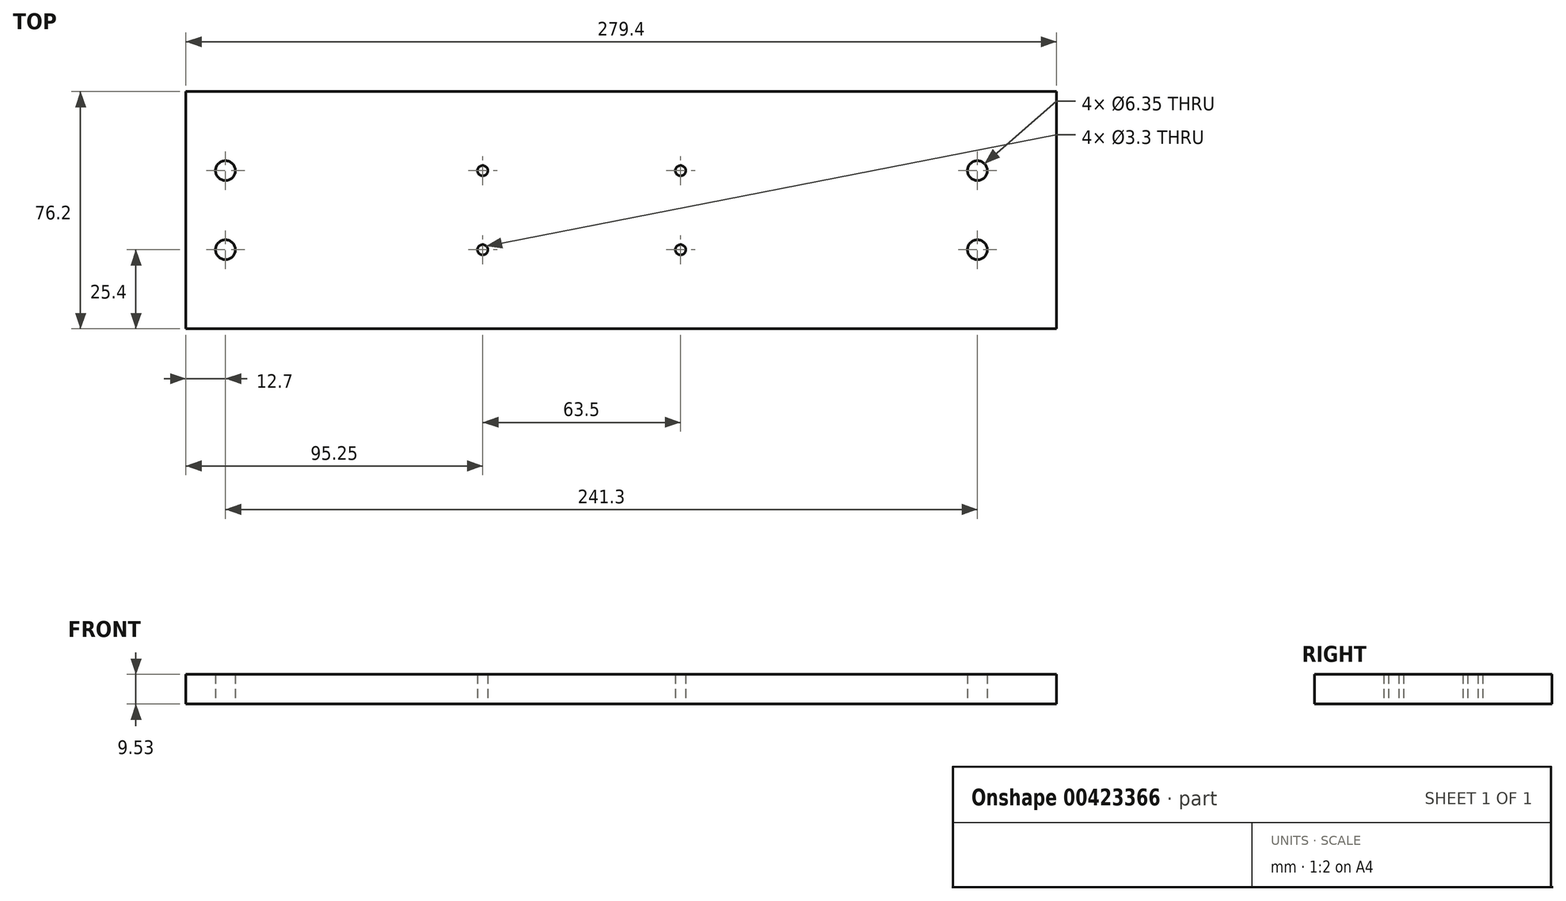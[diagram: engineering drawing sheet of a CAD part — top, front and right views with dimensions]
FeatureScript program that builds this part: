
annotation { "Feature Type Name" : "Feature", "Feature Type Description" : "" }
export const myFeature = defineFeature(function(context is Context, id is Id, definition is map)
    precondition{}
    {
        {
            var Q0;
            Q0=qCreatedBy(makeId("Top.planeOp"),FACE);
            var sketch = newSketch(context, id + "F0", { "sketchPlane" : qUnion([Q0])});
            skLineSegment(sketch, "E0.bottom", {"start": v(-139.7, 38.1) * mm, "end": v(139.7, 38.1) * mm});
            skLineSegment(sketch, "E0.top", {"start": v(-139.7, -38.1) * mm, "end": v(139.7, -38.1) * mm});
            skLineSegment(sketch, "E0.left", {"start": v(-139.7, 38.1) * mm, "end": v(-139.7, -38.1) * mm});
            skLineSegment(sketch, "E0.right", {"start": v(139.7, 38.1) * mm, "end": v(139.7, -38.1) * mm});
            skLineSegment(sketch, "E1.bottom", {"start": v(-127, 12.7) * mm, "end": v(114.3, 12.7) * mm, "construction": true});
            skLineSegment(sketch, "E1.top", {"start": v(-127, -12.7) * mm, "end": v(114.3, -12.7) * mm, "construction": true});
            skLineSegment(sketch, "E1.left", {"start": v(-127, 12.7) * mm, "end": v(-127, -12.7) * mm, "construction": true});
            skLineSegment(sketch, "E1.right", {"start": v(114.3, 12.7) * mm, "end": v(114.3, -12.7) * mm, "construction": true});
            skCircle(sketch, "E2", {"center": v(-127, 12.7) * mm, "radius": 3.17 * mm});
            skCircle(sketch, "E3", {"center": v(-127, -12.7) * mm, "radius": 3.17 * mm});
            skCircle(sketch, "E4", {"center": v(114.3, 12.7) * mm, "radius": 3.18 * mm});
            skCircle(sketch, "E5", {"center": v(114.3, -12.7) * mm, "radius": 3.18 * mm});
            skCircle(sketch, "E6", {"center": v(-44.45, 12.7) * mm, "radius": 1.65 * mm});
            skCircle(sketch, "E7", {"center": v(-44.45, -12.7) * mm, "radius": 1.65 * mm});
            skCircle(sketch, "E8", {"center": v(19.05, 12.7) * mm, "radius": 1.65 * mm});
            skCircle(sketch, "E9", {"center": v(19.05, -12.7) * mm, "radius": 1.65 * mm});
            skSolve(sketch);
        }
        {
            var Q0;
            Q0 = qSketchRegion(id + "F0", true);
            extrude(context, id + "F1", {"entities" : qUnion([Q0]), "depth" : 9.52 * mm});
        }
    });
